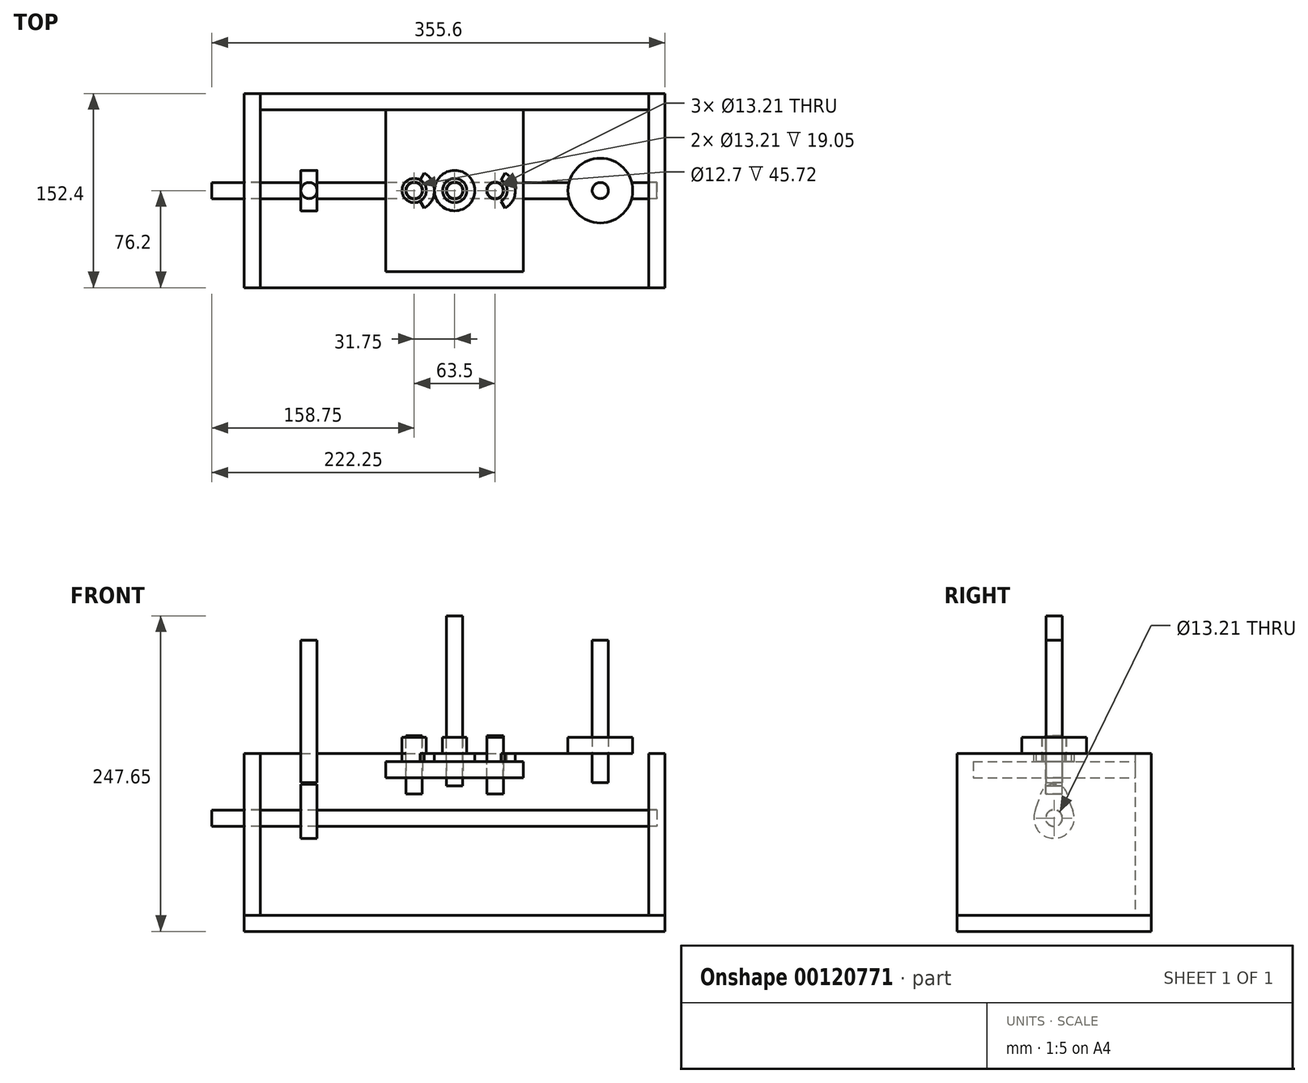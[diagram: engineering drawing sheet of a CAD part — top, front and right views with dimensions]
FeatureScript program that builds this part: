
annotation { "Feature Type Name" : "Feature", "Feature Type Description" : "" }
export const myFeature = defineFeature(function(context is Context, id is Id, definition is map)
    precondition{}
    {
        {
            var Q0;
            Q0=qCreatedBy(makeId("Top.planeOp"),FACE);
            var sketch = newSketch(context, id + "F0", { "sketchPlane" : qUnion([Q0])});
            skLineSegment(sketch, "E0.bottom", {"start": v(-165.1, 76.2) * mm, "end": v(165.1, 76.2) * mm});
            skLineSegment(sketch, "E0.top", {"start": v(-165.1, -76.2) * mm, "end": v(165.1, -76.2) * mm});
            skLineSegment(sketch, "E0.left", {"start": v(-165.1, 76.2) * mm, "end": v(-165.1, -76.2) * mm});
            skLineSegment(sketch, "E0.right", {"start": v(165.1, 76.2) * mm, "end": v(165.1, -76.2) * mm});
            skLineSegment(sketch, "E1", {"start": v(0, 76.2) * mm, "end": v(0, -76.2) * mm, "construction": true});
            skPoint(sketch, "E2", {"position": v(0, 0) * mm});
            skPoint(sketch, "E2.positionSnap0", {"position": v(0, 0) * mm});
            skLineSegment(sketch, "E3", {"start": v(-152.4, 76.2) * mm, "end": v(-152.4, -76.2) * mm});
            skLineSegment(sketch, "E4", {"start": v(152.4, 76.2) * mm, "end": v(152.4, -76.2) * mm});
            skLineSegment(sketch, "E5", {"start": v(-152.4, 63.5) * mm, "end": v(152.4, 63.5) * mm});
            skLineSegment(sketch, "E6", {"start": v(152.4, -63.5) * mm, "end": v(-152.4, -63.5) * mm});
            skSolve(sketch);
        }
        {
            var Q0;
            {var subQ5=sQuery(id+"F0.wireOp",EDGE,"E5");Q0=makeQuery(id+"F0.imprint","IMPRINT",FACE,{"disambiguationData":[TD([[makeQuery(id+"F0.imprint","IMPRINT",EDGE,{"derivedFrom":subQ5}),1.0]])]});}
            var Q1;
            {var subQ4=sQuery(id+"F0.wireOp",EDGE,"E0.left");Q1=makeQuery(id+"F0.imprint","IMPRINT",FACE,{"disambiguationData":[TD([[makeQuery(id+"F0.imprint","IMPRINT",EDGE,{"derivedFrom":subQ4}),1.0]])]});}
            var Q2;
            {var subQ0=sQuery(id+"F0.wireOp",EDGE,"E5");Q2=makeQuery(id+"F0.imprint","IMPRINT",FACE,{"disambiguationData":[TD([[makeQuery(id+"F0.imprint","IMPRINT",EDGE,{"derivedFrom":subQ0}),-1.0]])]});}
            var Q3;
            {var subQ5=sQuery(id+"F0.wireOp",EDGE,"E6");Q3=makeQuery(id+"F0.imprint","IMPRINT",FACE,{"disambiguationData":[TD([[makeQuery(id+"F0.imprint","IMPRINT",EDGE,{"derivedFrom":subQ5}),1.0]])]});}
            var Q4;
            {var subQ4=sQuery(id+"F0.wireOp",EDGE,"E0.right");Q4=makeQuery(id+"F0.imprint","IMPRINT",FACE,{"disambiguationData":[TD([[makeQuery(id+"F0.imprint","IMPRINT",EDGE,{"derivedFrom":subQ4}),-1.0]])]});}
            extrude(context, id + "F1", {"entities" : qUnion([Q0, Q1, Q2, Q3, Q4]), "oppositeDirection" : true, "depth" : 12.7 * mm});
        }
        {
            var Q0;
            {var subQ5=sQuery(id+"F0.wireOp",EDGE,"E5");Q0=makeQuery(id+"F0.imprint","IMPRINT",FACE,{"disambiguationData":[TD([[makeQuery(id+"F0.imprint","IMPRINT",EDGE,{"derivedFrom":subQ5}),1.0]])]});}
            extrude(context, id + "F2", {"entities" : qUnion([Q0]), "depth" : 127 * mm});
        }
        {
            var Q0;
            {var subQ4=sQuery(id+"F0.wireOp",EDGE,"E0.left");Q0=makeQuery(id+"F0.imprint","IMPRINT",FACE,{"disambiguationData":[TD([[makeQuery(id+"F0.imprint","IMPRINT",EDGE,{"derivedFrom":subQ4}),1.0]])]});}
            extrude(context, id + "F3", {"entities" : qUnion([Q0]), "depth" : 127 * mm});
        }
        {
            var Q0;
            {var subQ4=sQuery(id+"F0.wireOp",EDGE,"E0.right");Q0=makeQuery(id+"F0.imprint","IMPRINT",FACE,{"disambiguationData":[TD([[makeQuery(id+"F0.imprint","IMPRINT",EDGE,{"derivedFrom":subQ4}),-1.0]])]});}
            extrude(context, id + "F4", {"entities" : qUnion([Q0]), "depth" : 127 * mm});
        }
        {
            var Q0;
            Q0=makeQuery(id+"F1.opExtrude","CAP_FACE",FACE,{"disambiguationData":[OSD([sQuery(id+"F0.wireOp",EDGE,"E0.bottom"),sQuery(id+"F0.wireOp",EDGE,"E0.top"),sQuery(id+"F0.wireOp",EDGE,"E0.left"),sQuery(id+"F0.wireOp",EDGE,"E0.right")])],"isStart":false});
            extrude(context, id + "F5", {"entities" : qUnion([Q0]), "oppositeDirection" : true, "depth" : 152.4 * mm, "hasSecondDirection" : true, "secondDirectionOppositeDirection" : true, "secondDirectionDepth" : 139.7 * mm});
        }
        {
            var Q0;
            Q0=makeQuery(id+"F5.opExtrude","CAP_FACE",FACE,{"disambiguationData":[OSD([sQuery(id+"F0.wireOp",EDGE,"E0.bottom"),sQuery(id+"F0.wireOp",EDGE,"E0.top"),sQuery(id+"F0.wireOp",EDGE,"E0.left"),sQuery(id+"F0.wireOp",EDGE,"E0.right")])],"isStart":false});
            var sketch = newSketch(context, id + "F6", { "sketchPlane" : qUnion([Q0])});
            skLineSegment(sketch, "E7", {"start": v(-165.1, 0) * mm, "end": v(165.1, 0) * mm, "construction": true});
            skCircle(sketch, "E8", {"center": v(0, 0) * mm, "radius": 50.8 * mm});
            skLineSegment(sketch, "E9", {"start": v(-165.1, 0) * mm, "end": v(-114.3, 0) * mm, "construction": true});
            skCircle(sketch, "E10", {"center": v(-114.3, 0) * mm, "radius": 25.4 * mm});
            skLineSegment(sketch, "E11", {"start": v(0, 0) * mm, "end": v(0, -50.8) * mm, "construction": true});
            skCircle(sketch, "E12.MirrorC", {"center": v(114.3, 0) * mm, "radius": 25.4 * mm});
            skLineSegment(sketch, "E13", {"start": v(-114.3, 25.4) * mm, "end": v(-114.3, -25.4) * mm, "construction": true});
            skLineSegment(sketch, "E14.MirrorCS", {"start": v(114.3, 25.4) * mm, "end": v(114.3, -25.4) * mm, "construction": true});
            skSolve(sketch);
        }
        {
            var Q0;
            Q0=makeQuery(id+"F6.imprint","IMPRINT",FACE,{"disambiguationData":[TD([[makeQuery(id+"F6.imprint","IMPRINT",EDGE,{"derivedFrom":sQuery(id+"F6.wireOp",EDGE,"E10")}),1.0]])]});
            var Q1;
            Q1=makeQuery(id+"F6.imprint","IMPRINT",FACE,{"disambiguationData":[TD([[makeQuery(id+"F6.imprint","IMPRINT",EDGE,{"derivedFrom":sQuery(id+"F6.wireOp",EDGE,"E8")}),1.0]])]});
            var Q2;
            Q2=makeQuery(id+"F6.imprint","IMPRINT",FACE,{"disambiguationData":[TD([[makeQuery(id+"F6.imprint","IMPRINT",EDGE,{"derivedFrom":sQuery(id+"F6.wireOp",EDGE,"E12.MirrorC")}),-1.0]])]});
            extrude(context, id + "F7", {"entities" : qUnion([Q0, Q1, Q2]), "operationType" : NewBodyOperationType.REMOVE, "oppositeDirection" : true, "depth" : 12.7 * mm});
        }
        {
            var Q0;
            Q0=makeQuery(id+"F3.opExtrude","SWEPT_FACE",FACE,{"disambiguationData":[OSD([sQuery(id+"F0.wireOp",EDGE,"E0.left")])]});
            var sketch = newSketch(context, id + "F8", { "sketchPlane" : qUnion([Q0])});
            skLineSegment(sketch, "E15", {"start": v(0, 127) * mm, "end": v(0, 0) * mm, "construction": true});
            skPoint(sketch, "E16", {"position": v(0, 76.2) * mm});
            skCircle(sketch, "E17", {"center": v(0, 76.2) * mm, "radius": 6.6 * mm});
            skCircle(sketch, "E18", {"center": v(0, 76.2) * mm, "radius": 6.35 * mm});
            skSolve(sketch);
        }
        {
            var Q0;
            Q0 = qSketchRegion(id + "F8", true);
            extrude(context, id + "F9", {"entities" : qUnion([Q0]), "operationType" : NewBodyOperationType.REMOVE, "oppositeDirection" : true, "depth" : 12.7 * mm});
        }
        {
            var Q0;
            Q0=makeQuery(id+"F4.opExtrude","SWEPT_FACE",FACE,{"disambiguationData":[OSD([sQuery(id+"F0.wireOp",EDGE,"E4")])]});
            var sketch = newSketch(context, id + "F10", { "sketchPlane" : qUnion([Q0])});
            skCircle(sketch, "E19.0", {"center": v(0, 76.2) * mm, "radius": 6.6 * mm});
            skSolve(sketch);
        }
        {
            var Q0;
            Q0=makeQuery(id+"F10.imprint","IMPRINT",FACE,{"disambiguationData":[TD([[makeQuery(id+"F10.imprint","IMPRINT",EDGE,{"derivedFrom":sQuery(id+"F10.wireOp",EDGE,"E19.0")}),1.0]])]});
            extrude(context, id + "F11", {"entities" : qUnion([Q0]), "operationType" : NewBodyOperationType.REMOVE, "oppositeDirection" : true, "depth" : 6.35 * mm});
        }
        {
            var Q0;
            Q0=makeQuery(id+"F9.boolean.opBoolean","SPLIT",FACE,{"disambiguationData":[TD([makeQuery(id+"F9.opExtrude","SWEPT_FACE",FACE,{"disambiguationData":[OSD([sQuery(id+"F8.wireOp",EDGE,"E18")])]})])],"derivedFrom":makeQuery(id+"F3.opExtrude","SWEPT_FACE",FACE,{"disambiguationData":[OSD([sQuery(id+"F0.wireOp",EDGE,"E0.left")])]})});
            extrude(context, id + "F12", {"entities" : qUnion([Q0]), "oppositeDirection" : true, "depth" : 323.85 * mm, "hasSecondDirection" : true, "secondDirectionOppositeDirection" : false, "secondDirectionDepth" : 25.4 * mm});
        }
        {
            var Q0;
            {var subQ1=sQuery(id+"F0.wireOp",EDGE,"E3");var subQ3=sQuery(id+"F0.wireOp",EDGE,"E0.bottom");Q0=makeQuery(id+"F9.boolean.opBoolean","SPLIT",FACE,{"disambiguationData":[TD([makeQuery(id+"F3.opExtrude","SWEPT_FACE",FACE,{"disambiguationData":[OSD([subQ3])]})])],"derivedFrom":makeQuery(id+"F3.opExtrude","SWEPT_FACE",FACE,{"disambiguationData":[OSD([subQ1])]})});}
            var sketch = newSketch(context, id + "F13", { "sketchPlane" : qUnion([Q0])});
            skArc(sketch, "E20", {"start": v(-14.39, 82.9) * mm, "mid": v(-0.36, 60.33) * mm, "end": v(14.67, 82.26) * mm});
            skArc(sketch, "E21", {"start": v(0, 81.28) * mm, "mid": v(6.2, 83.24) * mm, "end": v(10.15, 88.4) * mm, "construction": true});
            skLineSegment(sketch, "E22", {"start": v(0, 76.2) * mm, "end": v(-15.88, 76.2) * mm, "construction": true});
            skLineSegment(sketch, "E23", {"start": v(0, 76.2) * mm, "end": v(0, 92.07) * mm, "construction": true});
            skLineSegment(sketch, "E24", {"start": v(0, 76.2) * mm, "end": v(-14.39, 82.9) * mm, "construction": true});
            skLineSegment(sketch, "E25", {"start": v(-14.03, 84) * mm, "end": v(-10.25, 95.45) * mm});
            skLineSegment(sketch, "E26.MirrorCS", {"start": v(14.03, 84) * mm, "end": v(10.25, 95.45) * mm});
            skLineSegment(sketch, "E27.MirrorCS", {"start": v(0, 76.2) * mm, "end": v(14.39, 82.9) * mm, "construction": true});
            skArc(sketch, "E28.trimOffspring", {"start": v(10.25, 95.45) * mm, "mid": v(0, 102.87) * mm, "end": v(-10.25, 95.45) * mm});
            skArc(sketch, "E29", {"start": v(-14.67, 82.26) * mm, "mid": v(0.36, 60.33) * mm, "end": v(14.39, 82.9) * mm});
            skCircle(sketch, "E30.0", {"center": v(0, 76.2) * mm, "radius": 6.35 * mm});
            skPoint(sketch, "E31.visualSharp", {"position": v(-14.39, 82.9) * mm});
            skArc(sketch, "E31.filletArc", {"start": v(-14.67, 82.26) * mm, "mid": v(-14.34, 83.12) * mm, "end": v(-14.03, 84) * mm});
            skPoint(sketch, "E32.visualSharp", {"position": v(14.39, 82.9) * mm});
            skArc(sketch, "E32.filletArc", {"start": v(14.03, 84) * mm, "mid": v(14.34, 83.12) * mm, "end": v(14.67, 82.26) * mm});
            skSolve(sketch);
        }
        {
            var Q0;
            Q0 = qSketchRegion(id + "F13", true);
            var Q1;
            Q1 = qConstructionFilter(qBodyType(qCreatedBy(id + "F13" ,EDGE), BodyType.WIRE), ConstructionObject.NO);
            extrude(context, id + "F14", {"entities" : qUnion([Q0]), "surfaceEntities" : qUnion([Q1]), "depth" : 44.45 * mm, "hasSecondDirection" : true, "secondDirectionOppositeDirection" : false, "secondDirectionDepth" : 31.75 * mm});
        }
        {
            var Q0;
            Q0=makeQuery(id+"F5.opExtrude","CAP_FACE",FACE,{"disambiguationData":[OSD([sQuery(id+"F0.wireOp",EDGE,"E0.bottom"),sQuery(id+"F0.wireOp",EDGE,"E0.top"),sQuery(id+"F0.wireOp",EDGE,"E0.left"),sQuery(id+"F0.wireOp",EDGE,"E0.right")])],"isStart":true});
            var sketch = newSketch(context, id + "F15", { "sketchPlane" : qUnion([Q0])});
            skPoint(sketch, "E33.0", {"position": v(0, 0) * mm});
            skCircle(sketch, "E34", {"center": v(0, 0) * mm, "radius": 15.88 * mm});
            skLineSegment(sketch, "E35", {"start": v(0, 0) * mm, "end": v(31.75, 0) * mm, "construction": true});
            skLineSegment(sketch, "E36", {"start": v(0, 0) * mm, "end": v(-31.75, 0) * mm, "construction": true});
            skArc(sketch, "E37", {"start": v(-23.81, -13.75) * mm, "mid": v(-15.88, 0) * mm, "end": v(-23.81, 13.75) * mm});
            skCircle(sketch, "E38", {"center": v(-31.75, 0) * mm, "radius": 6.6 * mm});
            skCircle(sketch, "E39", {"center": v(0, 0) * mm, "radius": 6.6 * mm});
            skCircle(sketch, "E40", {"center": v(0, 0) * mm, "radius": 9.53 * mm});
            skCircle(sketch, "E41", {"center": v(-31.75, 0) * mm, "radius": 9.53 * mm});
            skLineSegment(sketch, "E42", {"start": v(-26.99, -8.25) * mm, "end": v(-23.81, -13.75) * mm});
            skLineSegment(sketch, "E43", {"start": v(-26.99, 8.25) * mm, "end": v(-23.81, 13.75) * mm});
            skLineSegment(sketch, "E44.MirrorCS", {"start": v(26.99, -8.25) * mm, "end": v(23.81, -13.75) * mm, "construction": true});
            skLineSegment(sketch, "E45.MirrorCS", {"start": v(26.99, 8.25) * mm, "end": v(23.81, 13.75) * mm, "construction": true});
            skCircle(sketch, "E46.MirrorC", {"center": v(31.75, 0) * mm, "radius": 9.53 * mm});
            skCircle(sketch, "E47.MirrorC", {"center": v(31.75, 0) * mm, "radius": 6.6 * mm});
            skArc(sketch, "E48.MirrorCS", {"start": v(23.81, -13.75) * mm, "mid": v(15.88, 0) * mm, "end": v(23.81, 13.75) * mm, "construction": true});
            skLineSegment(sketch, "E49", {"start": v(31.75, 0) * mm, "end": v(31.75, 6.6) * mm, "construction": true});
            skLineSegment(sketch, "E50.MirrorCS", {"start": v(36.51, 8.25) * mm, "end": v(39.69, 13.75) * mm});
            skLineSegment(sketch, "E51.MirrorCS", {"start": v(36.51, -8.25) * mm, "end": v(39.69, -13.75) * mm});
            skArc(sketch, "E52.MirrorCS", {"start": v(39.69, -13.75) * mm, "mid": v(47.62, 0) * mm, "end": v(39.69, 13.75) * mm});
            skSolve(sketch);
        }
        {
            var Q0;
            Q0=makeQuery(id+"F15.imprint","IMPRINT",FACE,{"disambiguationData":[TD([[makeQuery(id+"F15.imprint","IMPRINT",EDGE,{"derivedFrom":sQuery(id+"F15.wireOp",EDGE,"E38")}),-1.0]])]});
            var Q1;
            {var subQ0=sQuery(id+"F15.wireOp",EDGE,"E42");Q1=makeQuery(id+"F15.imprint","IMPRINT",FACE,{"disambiguationData":[TD([[makeQuery(id+"F15.imprint","IMPRINT",EDGE,{"derivedFrom":subQ0}),1.0]])]});}
            var Q2;
            Q2=makeQuery(id+"F15.imprint","IMPRINT",FACE,{"disambiguationData":[TD([[makeQuery(id+"F15.imprint","IMPRINT",EDGE,{"derivedFrom":sQuery(id+"F15.wireOp",EDGE,"E34")}),1.0]])]});
            var Q3;
            Q3=makeQuery(id+"F15.imprint","IMPRINT",FACE,{"disambiguationData":[TD([[makeQuery(id+"F15.imprint","IMPRINT",EDGE,{"derivedFrom":sQuery(id+"F15.wireOp",EDGE,"E39")}),-1.0]])]});
            var Q4;
            Q4=makeQuery(id+"F15.imprint","IMPRINT",FACE,{"disambiguationData":[TD([[makeQuery(id+"F15.imprint","IMPRINT",EDGE,{"derivedFrom":sQuery(id+"F15.wireOp",EDGE,"E47.MirrorC")}),1.0]])]});
            var Q5;
            {var subQ0=sQuery(id+"F15.wireOp",EDGE,"E50.MirrorCS");Q5=makeQuery(id+"F15.imprint","IMPRINT",FACE,{"disambiguationData":[TD([[makeQuery(id+"F15.imprint","IMPRINT",EDGE,{"derivedFrom":subQ0}),-1.0]])]});}
            extrude(context, id + "F16", {"entities" : qUnion([Q0, Q1, Q2, Q3, Q4, Q5]), "depth" : 6.35 * mm});
        }
        {
            var Q0;
            Q0=makeQuery(id+"F15.imprint","IMPRINT",FACE,{"disambiguationData":[TD([[makeQuery(id+"F15.imprint","IMPRINT",EDGE,{"derivedFrom":sQuery(id+"F15.wireOp",EDGE,"E38")}),-1.0]])]});
            var Q1;
            Q1=makeQuery(id+"F15.imprint","IMPRINT",FACE,{"disambiguationData":[TD([[makeQuery(id+"F15.imprint","IMPRINT",EDGE,{"derivedFrom":sQuery(id+"F15.wireOp",EDGE,"E39")}),-1.0]])]});
            var Q2;
            Q2=makeQuery(id+"F15.imprint","IMPRINT",FACE,{"disambiguationData":[TD([[makeQuery(id+"F15.imprint","IMPRINT",EDGE,{"derivedFrom":sQuery(id+"F15.wireOp",EDGE,"E47.MirrorC")}),1.0]])]});
            extrude(context, id + "F17", {"entities" : qUnion([Q0, Q1, Q2]), "operationType" : NewBodyOperationType.ADD, "oppositeDirection" : true, "depth" : 12.7 * mm});
        }
        {
            var Q0;
            Q0=makeQuery(id+"F2.opExtrude","SWEPT_FACE",FACE,{"disambiguationData":[OSD([sQuery(id+"F0.wireOp",EDGE,"E5")])]});
            var sketch = newSketch(context, id + "F18", { "sketchPlane" : qUnion([Q0])});
            skLineSegment(sketch, "E53", {"start": v(-15.88, 120.65) * mm, "end": v(-53.98, 120.65) * mm, "construction": true});
            skLineSegment(sketch, "E54.bottom", {"start": v(-53.98, 120.65) * mm, "end": v(53.98, 120.65) * mm});
            skLineSegment(sketch, "E54.top", {"start": v(-53.98, 107.95) * mm, "end": v(53.98, 107.95) * mm});
            skLineSegment(sketch, "E54.left", {"start": v(-53.98, 120.65) * mm, "end": v(-53.98, 107.95) * mm});
            skLineSegment(sketch, "E54.right", {"start": v(53.98, 120.65) * mm, "end": v(53.98, 107.95) * mm});
            skLineSegment(sketch, "E55", {"start": v(-190.5, 82.55) * mm, "end": v(158.75, 82.55) * mm, "construction": true});
            skSolve(sketch);
        }
        {
            var Q0;
            Q0=makeQuery(id+"F18.imprint","IMPRINT",FACE,{"disambiguationData":[TD([[makeQuery(id+"F18.imprint","IMPRINT",EDGE,{"derivedFrom":sQuery(id+"F18.wireOp",EDGE,"E54.bottom")}),-1.0]])]});
            extrude(context, id + "F19", {"entities" : qUnion([Q0]), "depth" : 127 * mm});
        }
        {
            var Q0;
            Q0=makeQuery(id+"F19.opExtrude","SWEPT_FACE",FACE,{"disambiguationData":[OSD([sQuery(id+"F18.wireOp",EDGE,"E54.top")])]});
            var sketch = newSketch(context, id + "F20", { "sketchPlane" : qUnion([Q0])});
            skCircle(sketch, "E56.0", {"center": v(-31.75, 0) * mm, "radius": 6.6 * mm});
            skCircle(sketch, "E57.0", {"center": v(0, 0) * mm, "radius": 6.6 * mm});
            skCircle(sketch, "E58.0", {"center": v(31.75, 0) * mm, "radius": 6.6 * mm});
            skSolve(sketch);
        }
        {
            var Q0;
            Q0 = qSketchRegion(id + "F20", true);
            extrude(context, id + "F21", {"entities" : qUnion([Q0]), "operationType" : NewBodyOperationType.REMOVE, "oppositeDirection" : true, "depth" : 12.7 * mm});
        }
        {
            var Q0;
            Q0=makeQuery(id+"F19.opExtrude","SWEPT_FACE",FACE,{"disambiguationData":[OSD([sQuery(id+"F18.wireOp",EDGE,"E54.top")])]});
            var sketch = newSketch(context, id + "F22", { "sketchPlane" : qUnion([Q0])});
            skCircle(sketch, "E59.0", {"center": v(-31.75, 0) * mm, "radius": 6.6 * mm, "construction": true});
            skCircle(sketch, "E60", {"center": v(-31.75, 0) * mm, "radius": 6.35 * mm});
            skCircle(sketch, "E61.MirrorC", {"center": v(31.75, 0) * mm, "radius": 6.35 * mm});
            skCircle(sketch, "E62.0", {"center": v(0, 0) * mm, "radius": 6.6 * mm, "construction": true});
            skCircle(sketch, "E63", {"center": v(0, 0) * mm, "radius": 6.35 * mm});
            skSolve(sketch);
        }
        {
            var Q0;
            Q0=makeQuery(id+"F22.imprint","IMPRINT",FACE,{"disambiguationData":[TD([[makeQuery(id+"F22.imprint","IMPRINT",EDGE,{"derivedFrom":sQuery(id+"F22.wireOp",EDGE,"E60")}),1.0]])]});
            var Q1;
            Q1=makeQuery(id+"F22.imprint","IMPRINT",FACE,{"disambiguationData":[TD([[makeQuery(id+"F22.imprint","IMPRINT",EDGE,{"derivedFrom":sQuery(id+"F22.wireOp",EDGE,"E61.MirrorC")}),-1.0]])]});
            extrude(context, id + "F23", {"entities" : qUnion([Q0, Q1]), "depth" : 12.7 * mm, "hasSecondDirection" : true, "secondDirectionOppositeDirection" : true, "secondDirectionDepth" : 33.02 * mm});
        }
        {
            var Q0;
            Q0=makeQuery(id+"F22.imprint","IMPRINT",FACE,{"disambiguationData":[TD([[makeQuery(id+"F22.imprint","IMPRINT",EDGE,{"derivedFrom":sQuery(id+"F22.wireOp",EDGE,"E63")}),1.0]])]});
            extrude(context, id + "F24", {"entities" : qUnion([Q0]), "depth" : 6.35 * mm, "hasSecondDirection" : true, "secondDirectionOppositeDirection" : true, "secondDirectionDepth" : 127 * mm});
        }
        {
            var Q0;
            Q0=makeQuery(id+"F5.opExtrude","CAP_FACE",FACE,{"disambiguationData":[OSD([sQuery(id+"F0.wireOp",EDGE,"E0.bottom"),sQuery(id+"F0.wireOp",EDGE,"E0.top"),sQuery(id+"F0.wireOp",EDGE,"E0.left"),sQuery(id+"F0.wireOp",EDGE,"E0.right")])],"isStart":false});
            var sketch = newSketch(context, id + "F25", { "sketchPlane" : qUnion([Q0])});
            skCircle(sketch, "E64.0", {"center": v(-114.3, 0) * mm, "radius": 25.4 * mm, "construction": true});
            skCircle(sketch, "E65", {"center": v(-114.3, 0) * mm, "radius": 6.35 * mm});
            skSolve(sketch);
        }
        {
            var Q0;
            Q0=makeQuery(id+"F25.imprint","IMPRINT",FACE,{"disambiguationData":[TD([[makeQuery(id+"F25.imprint","IMPRINT",EDGE,{"derivedFrom":sQuery(id+"F25.wireOp",EDGE,"E65")}),1.0]])]});
            extrude(context, id + "F26", {"entities" : qUnion([Q0]), "depth" : 76.2 * mm, "hasSecondDirection" : true, "secondDirectionOppositeDirection" : true, "secondDirectionDepth" : 35.56 * mm});
        }
        {
            var Q0;
            Q0=makeQuery(id+"F26.opExtrude","SWEPT_BODY",BODY,{"disambiguationData":[OSD([sQuery(id+"F25.wireOp",EDGE,"E65")])]});
            var Q1;
            Q1=qCreatedBy(makeId("Right.planeOp"),FACE);
            mirror(context, id + "F27", {"entities" : qUnion([Q0]), "mirrorPlane" : qUnion([Q1])});
        }
    });
